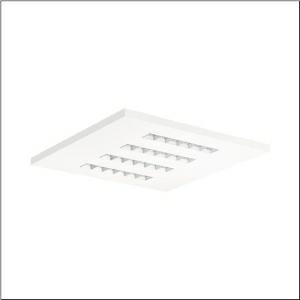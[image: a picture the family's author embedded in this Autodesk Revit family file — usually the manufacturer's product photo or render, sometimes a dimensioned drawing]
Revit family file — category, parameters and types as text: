
# Revit family: silica_21_square_51mx6mds34w
name_source: partatom
category: Lighting Fixtures
units: mm (PartAtom-declared; Revit-internal decimal feet)

## family parameters
Cut with Voids When Loaded = No
Host = Face
Light Source = No
Part Type = Normal
Room Calculation Point = No
Round Connector Dimension = Use Diameter
Shared = No

## types (1)
- --- (1 x LED, 4600 lm, 29.2 W, 3000K)
    Apparent Load = 29 VA
    CIE Flux Codes = 83 98 100 100 100
    Color Rendering = 80
    Color Temperature = 3000K
    Default Elevation = 1800 mm
    Description = Silica 21 Square, office luminaire, primary light control with lens, of PMMA, primary anti-glare with reflector, of PC, white, CAT 2 (L<= 3000cd/m²), light emission: direct distribution, primary light characteristic: symmetric, installation type: lay-in mounting, LED, rated luminous flux: 4.600lm, luminous efficacy: 158lm/W, light colour: 830, colour temperature: 3000K, control gear: DALI 2, with terminal, 5-pole, mains connection: 220..240V, AC, 50/60Hz, rated input power: 29.2W, luminaire housing, of sheet steel, coated, traffic white (RAL 9016), module: M600, length: 597mm, width: 597mm, height: 33mm, protection rating (complete): IP20, insulation class (complete): insulation class I (protective earthing), certification: CE, ENEC, VDE, permissible operating ambient temperature: -20..+40°C, standard: EN 50419, packaging unit: 1 piece
    Height = 0 mm  [stored 0 ft]
    Lamp = 1 x LED
    Lamp Light Flux = 4600 lm
    Lamp Power = 29.2 W
    Lamp count = 1
    Length = 597 mm
    Luminous efficacy = 158 lm/W
    Manufacturer = Siteco
    ModVariant = No
    Model = 51MX6MDS34W
    Mounting Place = Ceiling
    Mounting Type = Recessed
    Number of Poles = 1
    OnlyDefault = Yes
    Power Factor = 1
    Product Name = Silica 21 Square
    Product group = office luminaire | ceiling recessed
    ProductGroupID = 400
    Protection Class = Protection class I
    Protection Degree = IP 20
    RLX_Detail_Level = 1
    RLX_Emergency_Light_Flux = 0 lm
    RLX_Emergency_Type = 0
    RLX_Emergency_Type_DB = No
    RlxData = <blob elided: 18525 chars, md5=e32fca79>
    Socket = socket
    Standby Power = 0 W
    System Light Flux = 4600 lm
    System Power = 29 W
    Type Comments = factory setting: luminous flux: 100 % | dim-lin: 254 | 393 mA
    Type Image = l_1275220.jpg
    URL = http://relux.com
    VarID = @adj_088869
    Voltage = 0 V
    Weight = 0.00 kg
    Width = 597 mm

note: [stored X ft] marks values corroborated as IEEE doubles in the binary element streams (Revit-internal decimal feet)

## geometry (parser evidence)
native form markers: Blend x4, Sweep x10
no freeform markers — native parametric forms only
